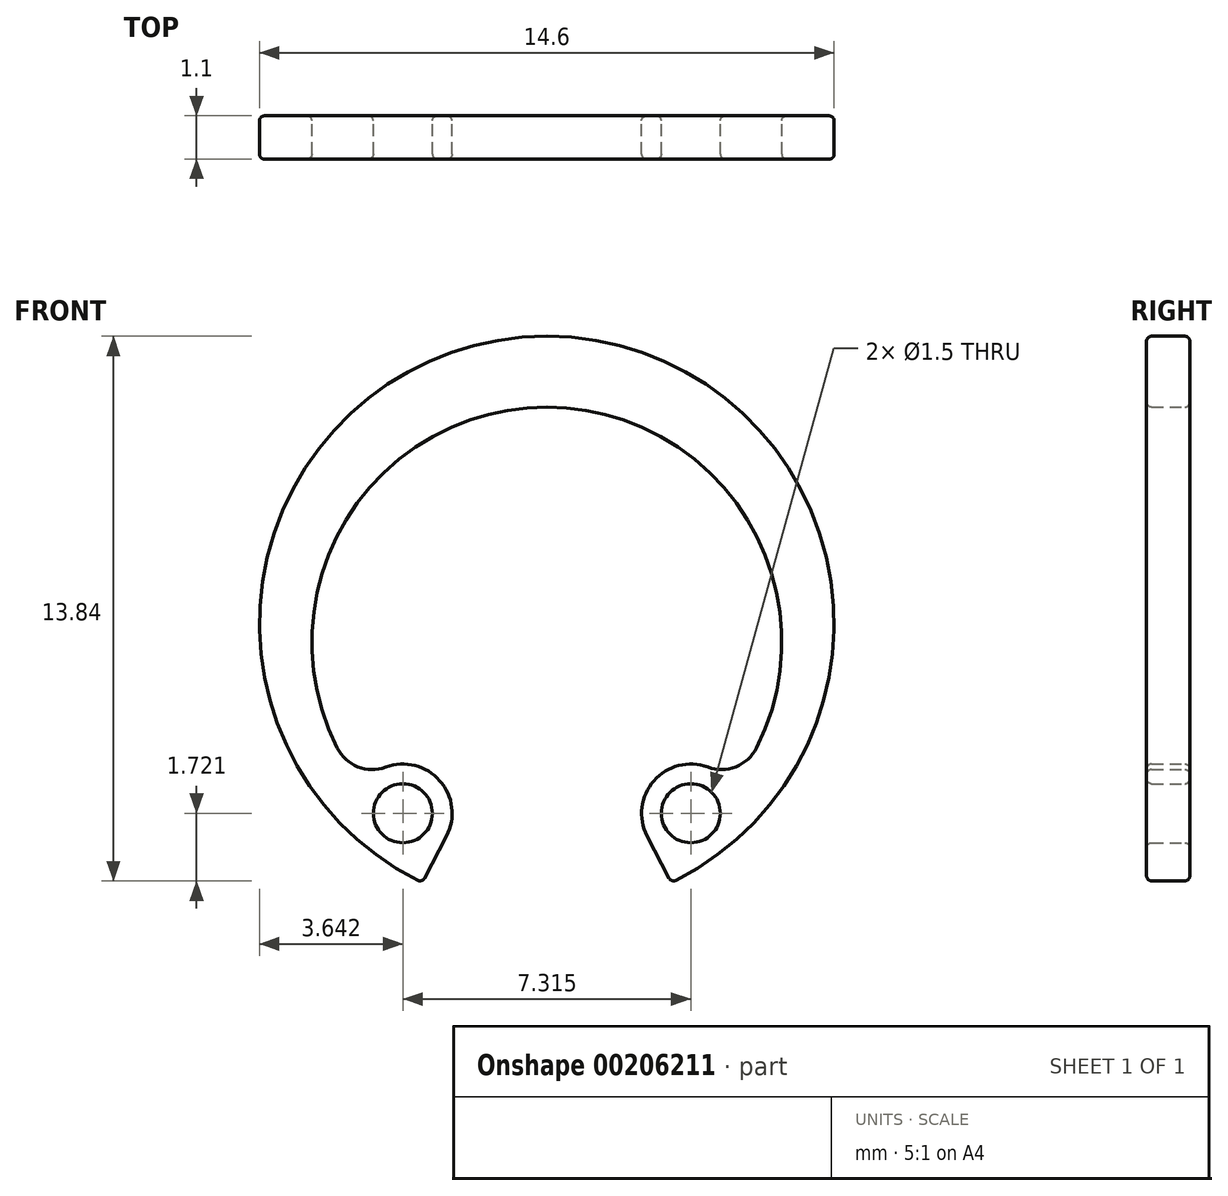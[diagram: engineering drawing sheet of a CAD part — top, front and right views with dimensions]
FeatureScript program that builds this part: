
annotation { "Feature Type Name" : "Feature", "Feature Type Description" : "" }
export const myFeature = defineFeature(function(context is Context, id is Id, definition is map)
    precondition{}
    {
        {
            var Q0;
            Q0=qCreatedBy(makeId("Front.planeOp"),FACE);
            var sketch = newSketch(context, id + "F0", { "sketchPlane" : qUnion([Q0])});
            skArc(sketch, "E0", {"start": v(3.16, -6.58) * mm, "mid": v(0, 7.3) * mm, "end": v(-3.16, -6.58) * mm});
            skPoint(sketch, "E1.second.point", {"position": v(0, -6) * mm});
            skPoint(sketch, "E1.third.point", {"position": v(5.48, -0.05) * mm});
            skLineSegment(sketch, "E2", {"start": v(-2.55, -5.4) * mm, "end": v(-3.16, -6.58) * mm});
            skLineSegment(sketch, "E3", {"start": v(2.55, -5.4) * mm, "end": v(3.16, -6.58) * mm});
            skLineSegment(sketch, "E4", {"start": v(-3.16, -6.58) * mm, "end": v(3.16, -6.58) * mm, "construction": true});
            skCircle(sketch, "E5", {"center": v(-3.66, -4.82) * mm, "radius": 0.75 * mm});
            skLineSegment(sketch, "E6", {"start": v(0, 1.94) * mm, "end": v(0, -8.92) * mm, "construction": true});
            skPoint(sketch, "E6.endSnap0", {"position": v(0, -6.58) * mm});
            skArc(sketch, "E7.0", {"start": v(-2.55, -5.4) * mm, "mid": v(-2.72, -4) * mm, "end": v(-4.1, -3.65) * mm});
            skArc(sketch, "E8.MirrorCS", {"start": v(2.55, -5.4) * mm, "mid": v(2.72, -4) * mm, "end": v(4.1, -3.65) * mm});
            skCircle(sketch, "E9.MirrorC", {"center": v(3.66, -4.82) * mm, "radius": 0.75 * mm});
            skArc(sketch, "E10.trimOffspring", {"start": v(5.33, -3.16) * mm, "mid": v(0, 5.5) * mm, "end": v(-5.33, -3.16) * mm});
            skPoint(sketch, "E11.orphan", {"position": v(0, -0.5) * mm});
            skPoint(sketch, "E12.visualSharp", {"position": v(-4.7, -4.14) * mm});
            skArc(sketch, "E12.filletArc", {"start": v(-5.33, -3.16) * mm, "mid": v(-4.8, -3.64) * mm, "end": v(-4.1, -3.65) * mm});
            skPoint(sketch, "E13.visualSharp", {"position": v(4.7, -4.14) * mm});
            skArc(sketch, "E13.filletArc", {"start": v(4.1, -3.65) * mm, "mid": v(4.8, -3.64) * mm, "end": v(5.33, -3.16) * mm});
            skSolve(sketch);
        }
        {
            var Q0;
            Q0=makeQuery(id+"F0.imprint","IMPRINT",FACE,{"disambiguationData":[TD([[makeQuery(id+"F0.imprint","IMPRINT",EDGE,{"derivedFrom":sQuery(id+"F0.wireOp",EDGE,"E0")}),1.0]])]});
            extrude(context, id + "F1", {"entities" : qUnion([Q0]), "depth" : 1.1 * mm});
        }
        {
            var Q0;
            Q0=makeQuery(id+"F1.opExtrude","CAP_FACE",FACE,{"disambiguationData":[OSD([sQuery(id+"F0.wireOp",EDGE,"E0"),sQuery(id+"F0.wireOp",EDGE,"E2"),sQuery(id+"F0.wireOp",EDGE,"E3"),sQuery(id+"F0.wireOp",EDGE,"E5"),sQuery(id+"F0.wireOp",EDGE,"E7.0"),sQuery(id+"F0.wireOp",EDGE,"E8.MirrorCS"),sQuery(id+"F0.wireOp",EDGE,"E9.MirrorC"),sQuery(id+"F0.wireOp",EDGE,"E10.trimOffspring"),sQuery(id+"F0.wireOp",EDGE,"E12.filletArc"),sQuery(id+"F0.wireOp",EDGE,"E13.filletArc")])],"isStart":false});
            var Q1;
            Q1=makeQuery(id+"F1.opExtrude","CAP_FACE",FACE,{"disambiguationData":[OSD([sQuery(id+"F0.wireOp",EDGE,"E0"),sQuery(id+"F0.wireOp",EDGE,"E2"),sQuery(id+"F0.wireOp",EDGE,"E3"),sQuery(id+"F0.wireOp",EDGE,"E5"),sQuery(id+"F0.wireOp",EDGE,"E7.0"),sQuery(id+"F0.wireOp",EDGE,"E8.MirrorCS"),sQuery(id+"F0.wireOp",EDGE,"E9.MirrorC"),sQuery(id+"F0.wireOp",EDGE,"E10.trimOffspring"),sQuery(id+"F0.wireOp",EDGE,"E12.filletArc"),sQuery(id+"F0.wireOp",EDGE,"E13.filletArc")])],"isStart":true});
            var Q2;
            Q2=makeQuery(id+"F1.opExtrude","SWEPT_EDGE",EDGE,{"disambiguationData":[OSD([sQuery(id+"F0.wireOp",EDGE,"E0"),sQuery(id+"F0.wireOp",EDGE,"E2")])]});
            var Q3;
            Q3=makeQuery(id+"F1.opExtrude","SWEPT_EDGE",EDGE,{"disambiguationData":[OSD([sQuery(id+"F0.wireOp",EDGE,"E0"),sQuery(id+"F0.wireOp",EDGE,"E3")])]});
            fillet(context, id + "F2", {"entities" : qUnion([Q0, Q1, Q2, Q3]), "radius" : 0.13 * mm, "tangentPropagation" : true, "allowEdgeOverflow" : false});
        }
    });
